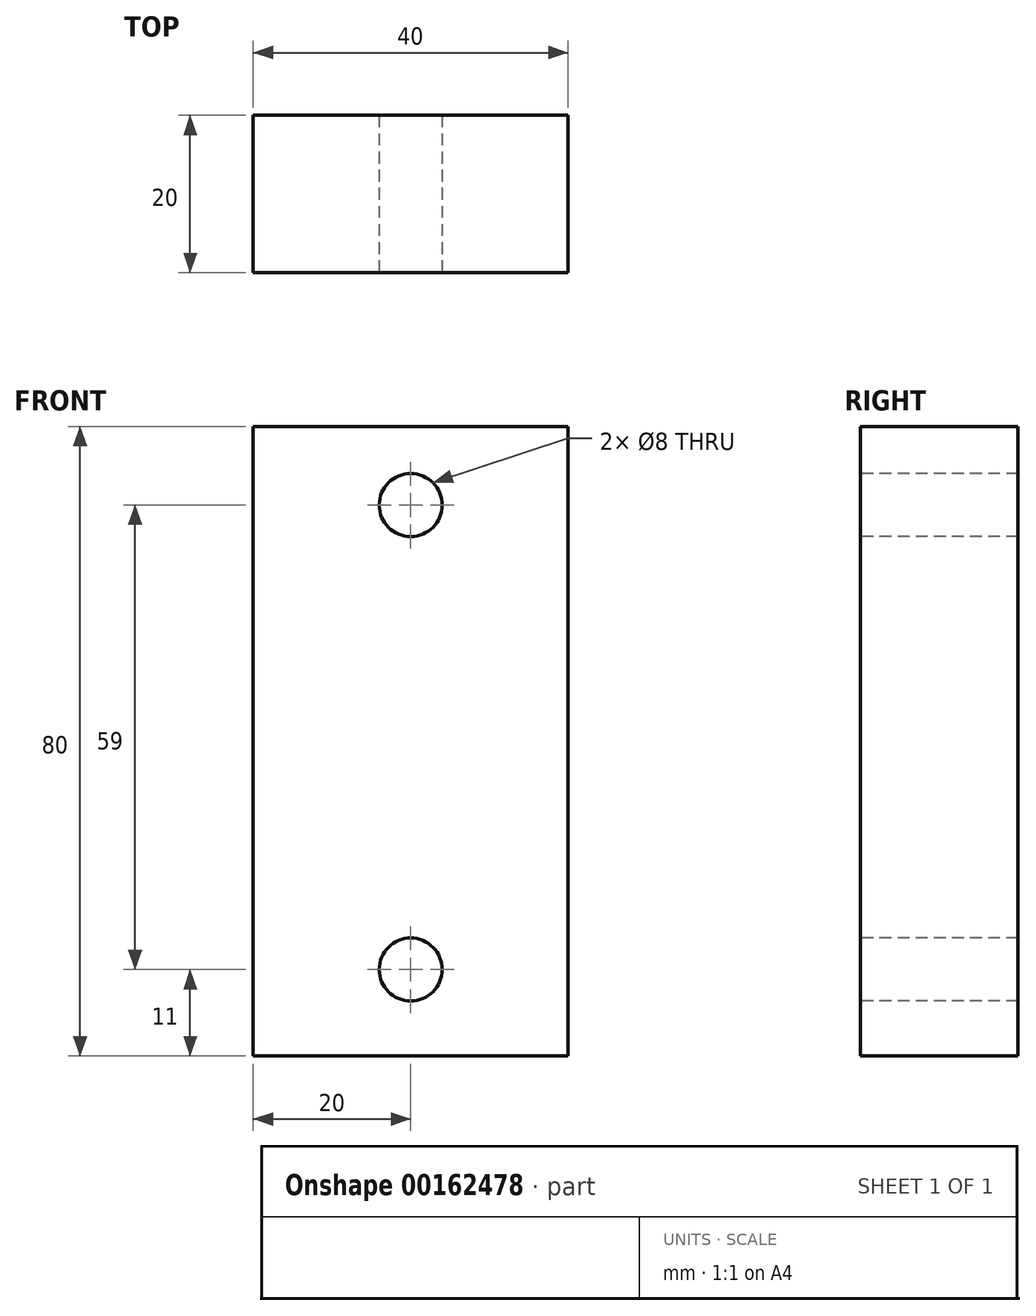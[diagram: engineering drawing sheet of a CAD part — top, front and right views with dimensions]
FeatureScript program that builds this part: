
annotation { "Feature Type Name" : "Feature", "Feature Type Description" : "" }
export const myFeature = defineFeature(function(context is Context, id is Id, definition is map)
    precondition{}
    {
        {
            var Q0;
            Q0=qCreatedBy(makeId("Top.planeOp"),FACE);
            var sketch = newSketch(context, id + "F0", { "sketchPlane" : qUnion([Q0])});
            skLineSegment(sketch, "E0.bottom", {"start": v(20, 10) * mm, "end": v(-20, 10) * mm});
            skLineSegment(sketch, "E0.top", {"start": v(20, -10) * mm, "end": v(-20, -10) * mm});
            skLineSegment(sketch, "E0.left", {"start": v(20, 10) * mm, "end": v(20, -10) * mm});
            skLineSegment(sketch, "E0.right", {"start": v(-20, 10) * mm, "end": v(-20, -10) * mm});
            skPoint(sketch, "E0.middle", {"position": v(0, 0) * mm});
            skSolve(sketch);
        }
        {
            var Q0;
            Q0=makeQuery(id+"F0.imprint","IMPRINT",FACE,{"disambiguationData":[TD([[makeQuery(id+"F0.imprint","IMPRINT",EDGE,{"derivedFrom":sQuery(id+"F0.wireOp",EDGE,"E0.bottom")}),1.0]])]});
            extrude(context, id + "F1", {"entities" : qUnion([Q0]), "depth" : 80 * mm});
        }
        {
            var Q0;
            Q0=makeQuery(id+"F1.opExtrude","SWEPT_FACE",FACE,{"disambiguationData":[OSD([sQuery(id+"F0.wireOp",EDGE,"E0.top")])]});
            var sketch = newSketch(context, id + "F2", { "sketchPlane" : qUnion([Q0])});
            skCircle(sketch, "E1", {"center": v(0, 11) * mm, "radius": 3.5 * mm});
            skCircle(sketch, "E2", {"center": v(0, 70) * mm, "radius": 4 * mm});
            skSolve(sketch);
        }
        {
            var Q0;
            Q0=sQuery(id+"F2.wireOp",VERTEX,"E2.center");
            var Q1;
            Q1=sQuery(id+"F2.wireOp",VERTEX,"E1.center");
            var Q2;
            Q2=makeQuery(id+"F1.opExtrude","SWEPT_BODY",BODY,{"disambiguationData":[OSD([sQuery(id+"F0.wireOp",EDGE,"E0.bottom"),sQuery(id+"F0.wireOp",EDGE,"E0.top"),sQuery(id+"F0.wireOp",EDGE,"E0.left"),sQuery(id+"F0.wireOp",EDGE,"E0.right")])]});
            hole(context, id + "F3", {"style" : HoleStyle.SIMPLE, "endStyle" : HoleEndStyle.THROUGH, "holeDiameter" : 8 * mm, "locations" : qUnion([Q0, Q1]), "scope" : qUnion([Q2]), "isTappedThrough" : true});
        }
    });
